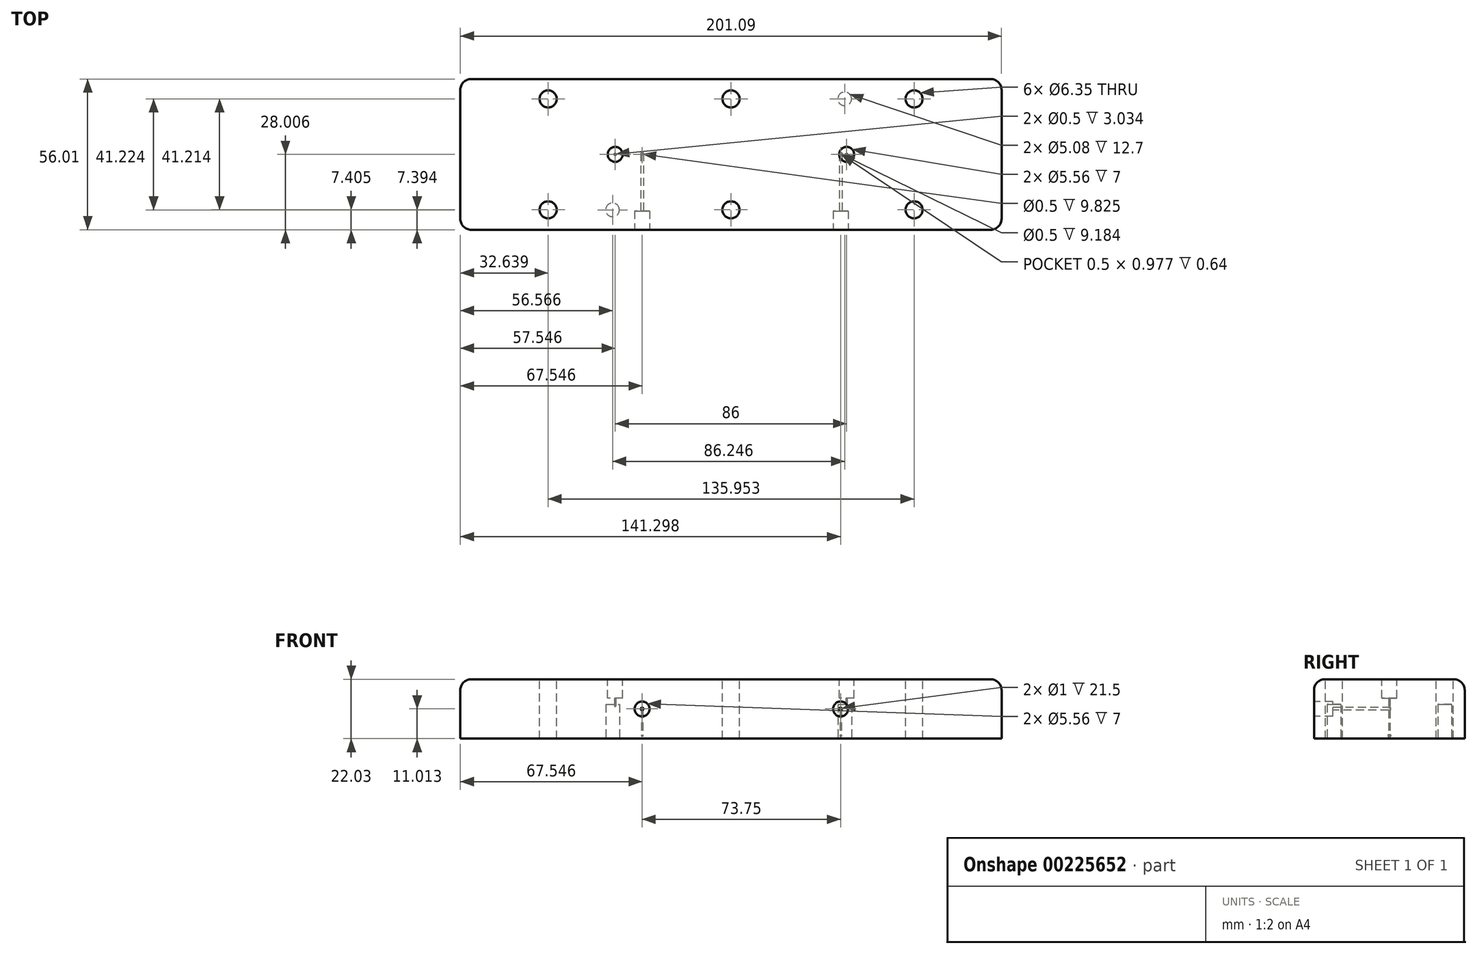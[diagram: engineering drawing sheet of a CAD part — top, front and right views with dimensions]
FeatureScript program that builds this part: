
annotation { "Feature Type Name" : "Feature", "Feature Type Description" : "" }
export const myFeature = defineFeature(function(context is Context, id is Id, definition is map)
    precondition{}
    {
        {
            var Q0;
            Q0=qCreatedBy(makeId("Top.planeOp"),FACE);
            var sketch = newSketch(context, id + "F0", { "sketchPlane" : qUnion([Q0])});
            skLineSegment(sketch, "E0.bottom", {"start": v(4.06, 0) * mm, "end": v(197.03, 0) * mm});
            skLineSegment(sketch, "E0.top", {"start": v(4.06, -56) * mm, "end": v(197.03, -56) * mm});
            skLineSegment(sketch, "E0.left", {"start": v(0, -4.06) * mm, "end": v(0, -51.94) * mm});
            skLineSegment(sketch, "E0.right", {"start": v(201.1, -4.06) * mm, "end": v(201.1, -51.94) * mm});
            skLineSegment(sketch, "E1.bottom", {"start": v(0, 0) * mm, "end": v(201.1, 0) * mm, "construction": true});
            skLineSegment(sketch, "E1.top", {"start": v(0, -7.4) * mm, "end": v(201.1, -7.4) * mm, "construction": true});
            skLineSegment(sketch, "E1.left", {"start": v(0, 0) * mm, "end": v(0, -7.4) * mm, "construction": true});
            skLineSegment(sketch, "E1.right", {"start": v(201.1, 0) * mm, "end": v(201.1, -7.4) * mm, "construction": true});
            skLineSegment(sketch, "E2.bottom", {"start": v(0, 0) * mm, "end": v(32.64, 0) * mm, "construction": true});
            skLineSegment(sketch, "E2.top", {"start": v(0, -56) * mm, "end": v(32.64, -56) * mm, "construction": true});
            skLineSegment(sketch, "E2.left", {"start": v(0, 0) * mm, "end": v(0, -56) * mm, "construction": true});
            skLineSegment(sketch, "E2.right", {"start": v(32.64, 0) * mm, "end": v(32.64, -56) * mm, "construction": true});
            skLineSegment(sketch, "E3.bottom", {"start": v(0, 0) * mm, "end": v(168.6, 0) * mm, "construction": true});
            skLineSegment(sketch, "E3.top", {"start": v(0, -56) * mm, "end": v(168.6, -56) * mm, "construction": true});
            skLineSegment(sketch, "E3.right", {"start": v(168.6, 0) * mm, "end": v(168.6, -56) * mm, "construction": true});
            skLineSegment(sketch, "E4.bottom", {"start": v(0, 0) * mm, "end": v(100.57, 0) * mm, "construction": true});
            skLineSegment(sketch, "E4.top", {"start": v(0, -56) * mm, "end": v(100.57, -56) * mm, "construction": true});
            skLineSegment(sketch, "E4.right", {"start": v(100.57, 0) * mm, "end": v(100.57, -56) * mm, "construction": true});
            skLineSegment(sketch, "E5.top", {"start": v(0, -48.6) * mm, "end": v(201.1, -48.6) * mm, "construction": true});
            skLineSegment(sketch, "E5.left", {"start": v(0, 0) * mm, "end": v(0, -48.6) * mm, "construction": true});
            skLineSegment(sketch, "E5.right", {"start": v(201.1, 0) * mm, "end": v(201.1, -48.6) * mm, "construction": true});
            skLineSegment(sketch, "E6.bottom", {"start": v(0, 0) * mm, "end": v(52.5, 0) * mm, "construction": true});
            skLineSegment(sketch, "E6.top", {"start": v(0, -56) * mm, "end": v(52.5, -56) * mm, "construction": true});
            skLineSegment(sketch, "E6.right", {"start": v(52.5, 0) * mm, "end": v(52.5, -56) * mm, "construction": true});
            skCircle(sketch, "E7", {"center": v(32.64, -7.4) * mm, "radius": 3.18 * mm});
            skCircle(sketch, "E8", {"center": v(100.57, -7.4) * mm, "radius": 3.18 * mm});
            skCircle(sketch, "E9", {"center": v(168.6, -7.4) * mm, "radius": 3.18 * mm});
            skCircle(sketch, "E10", {"center": v(168.6, -48.6) * mm, "radius": 3.18 * mm});
            skCircle(sketch, "E11", {"center": v(100.55, -48.6) * mm, "radius": 3.18 * mm});
            skCircle(sketch, "E12", {"center": v(32.64, -48.6) * mm, "radius": 3.18 * mm});
            skLineSegment(sketch, "E13.bottom", {"start": v(0, 0) * mm, "end": v(138.75, 0) * mm, "construction": true});
            skLineSegment(sketch, "E13.top", {"start": v(0, -56) * mm, "end": v(138.75, -56) * mm, "construction": true});
            skLineSegment(sketch, "E13.right", {"start": v(138.75, 0) * mm, "end": v(138.75, -56) * mm, "construction": true});
            skLineSegment(sketch, "E14.top", {"start": v(0, -56) * mm, "end": v(201.1, -56) * mm, "construction": true});
            skLineSegment(sketch, "E14.right", {"start": v(201.1, 0) * mm, "end": v(201.1, -56) * mm, "construction": true});
            skPoint(sketch, "E15.visualSharp", {"position": v(201.1, 0) * mm});
            skArc(sketch, "E15.filletArc", {"start": v(201.1, -4.06) * mm, "mid": v(199.9, -1.2) * mm, "end": v(197.03, 0) * mm});
            skPoint(sketch, "E16.visualSharp", {"position": v(0, -56) * mm});
            skArc(sketch, "E16.filletArc", {"start": v(0, -51.94) * mm, "mid": v(1.2, -54.82) * mm, "end": v(4.06, -56) * mm});
            skPoint(sketch, "E17.visualSharp", {"position": v(201.1, -56) * mm});
            skArc(sketch, "E17.filletArc", {"start": v(197.03, -56) * mm, "mid": v(199.9, -54.82) * mm, "end": v(201.1, -51.94) * mm});
            skPoint(sketch, "E18.visualSharp", {"position": v(0, 0) * mm});
            skArc(sketch, "E18.filletArc", {"start": v(4.06, 0) * mm, "mid": v(1.2, -1.2) * mm, "end": v(0, -4.06) * mm});
            skSolve(sketch);
        }
        {
            var Q0;
            Q0=qSketchRegion(id+"F0",true);
            extrude(context, id + "F1", {"entities" : qUnion([Q0]), "oppositeDirection" : true, "depth" : 22.03 * mm});
        }
        {
            var Q0;
            Q0=makeQuery(id+"F1.opExtrude","CAP_FACE",FACE,{"disambiguationData":[OSD([sQuery(id+"F0.wireOp",EDGE,"E0.bottom"),sQuery(id+"F0.wireOp",EDGE,"E0.top"),sQuery(id+"F0.wireOp",EDGE,"E0.left"),sQuery(id+"F0.wireOp",EDGE,"E0.right"),sQuery(id+"F0.wireOp",EDGE,"E7"),sQuery(id+"F0.wireOp",EDGE,"E8"),sQuery(id+"F0.wireOp",EDGE,"E9"),sQuery(id+"F0.wireOp",EDGE,"E10"),sQuery(id+"F0.wireOp",EDGE,"E11"),sQuery(id+"F0.wireOp",EDGE,"E12")])],"isStart":false});
            var sketch = newSketch(context, id + "F2", { "sketchPlane" : qUnion([Q0])});
            skLineSegment(sketch, "E19.bottom", {"start": v(4.06, 0) * mm, "end": v(201.1, 0) * mm, "construction": true});
            skLineSegment(sketch, "E19.top", {"start": v(4.06, 7.4) * mm, "end": v(201.1, 7.4) * mm, "construction": true});
            skLineSegment(sketch, "E19.left", {"start": v(4.06, 0) * mm, "end": v(4.06, 7.4) * mm, "construction": true});
            skLineSegment(sketch, "E19.right", {"start": v(201.1, 0) * mm, "end": v(201.1, 7.4) * mm, "construction": true});
            skLineSegment(sketch, "E20.top", {"start": v(4.06, 48.62) * mm, "end": v(201.1, 48.62) * mm, "construction": true});
            skLineSegment(sketch, "E20.left", {"start": v(4.06, 0) * mm, "end": v(4.06, 48.62) * mm, "construction": true});
            skLineSegment(sketch, "E20.right", {"start": v(201.1, 0) * mm, "end": v(201.1, 48.62) * mm, "construction": true});
            skLineSegment(sketch, "E21.bottom", {"start": v(4.06, 0) * mm, "end": v(56.57, 0) * mm, "construction": true});
            skLineSegment(sketch, "E21.top", {"start": v(4.06, 56) * mm, "end": v(56.57, 56) * mm, "construction": true});
            skLineSegment(sketch, "E21.left", {"start": v(4.06, 0) * mm, "end": v(4.06, 56) * mm, "construction": true});
            skLineSegment(sketch, "E21.right", {"start": v(56.57, 0) * mm, "end": v(56.57, 56) * mm, "construction": true});
            skLineSegment(sketch, "E22.bottom", {"start": v(4.06, 0) * mm, "end": v(142.81, 0) * mm, "construction": true});
            skLineSegment(sketch, "E22.top", {"start": v(4.06, 56) * mm, "end": v(142.81, 56) * mm, "construction": true});
            skLineSegment(sketch, "E22.right", {"start": v(142.81, 0) * mm, "end": v(142.81, 56) * mm, "construction": true});
            skCircle(sketch, "E23", {"center": v(56.57, 48.62) * mm, "radius": 2.54 * mm});
            skCircle(sketch, "E24", {"center": v(142.81, 7.4) * mm, "radius": 2.54 * mm});
            skSolve(sketch);
        }
        {
            var Q0;
            Q0=qSketchRegion(id+"F2",true);
            extrude(context, id + "F3", {"entities" : qUnion([Q0]), "operationType" : NewBodyOperationType.REMOVE, "oppositeDirection" : true, "depth" : 12.7 * mm});
        }
        {
            var Q0;
            Q0=makeQuery(id+"F1.opExtrude","CAP_FACE",FACE,{"disambiguationData":[OSD([sQuery(id+"F0.wireOp",EDGE,"E0.bottom"),sQuery(id+"F0.wireOp",EDGE,"E0.top"),sQuery(id+"F0.wireOp",EDGE,"E0.left"),sQuery(id+"F0.wireOp",EDGE,"E0.right"),sQuery(id+"F0.wireOp",EDGE,"E7"),sQuery(id+"F0.wireOp",EDGE,"E8"),sQuery(id+"F0.wireOp",EDGE,"E9"),sQuery(id+"F0.wireOp",EDGE,"E10"),sQuery(id+"F0.wireOp",EDGE,"E11"),sQuery(id+"F0.wireOp",EDGE,"E12"),sQuery(id+"F0.wireOp",EDGE,"E15.filletArc"),sQuery(id+"F0.wireOp",EDGE,"E16.filletArc"),sQuery(id+"F0.wireOp",EDGE,"E17.filletArc"),sQuery(id+"F0.wireOp",EDGE,"E18.filletArc")])],"isStart":false});
            var sketch = newSketch(context, id + "F4", { "sketchPlane" : qUnion([Q0])});
            skLineSegment(sketch, "E25.bottom", {"start": v(143.55, 35.5) * mm, "end": v(57.55, 35.5) * mm, "construction": true});
            skLineSegment(sketch, "E25.top", {"start": v(143.55, 20.5) * mm, "end": v(57.55, 20.5) * mm, "construction": true});
            skLineSegment(sketch, "E25.left", {"start": v(143.55, 35.5) * mm, "end": v(143.55, 20.5) * mm, "construction": true});
            skLineSegment(sketch, "E25.right", {"start": v(57.55, 35.5) * mm, "end": v(57.55, 20.5) * mm, "construction": true});
            skPoint(sketch, "E25.middle", {"position": v(100.55, 28) * mm});
            skPoint(sketch, "E25.middle.positionSnap0", {"position": v(100.55, 56) * mm});
            skPoint(sketch, "E25.middle.positionSnap1", {"position": v(0, 28) * mm});
            skPoint(sketch, "E25.centerSnap0", {"position": v(100.55, 56) * mm});
            skPoint(sketch, "E25.centerSnap1", {"position": v(0, 28) * mm});
            skCircle(sketch, "E26", {"center": v(143.55, 28) * mm, "radius": 0.25 * mm, "construction": true});
            skCircle(sketch, "E27", {"center": v(57.55, 28) * mm, "radius": 0.25 * mm, "construction": true});
            skLineSegment(sketch, "E28.bottom", {"start": v(57.55, 35.5) * mm, "end": v(67.55, 35.5) * mm, "construction": true});
            skLineSegment(sketch, "E28.top", {"start": v(57.55, 20.5) * mm, "end": v(67.55, 20.5) * mm, "construction": true});
            skLineSegment(sketch, "E28.right", {"start": v(67.55, 35.5) * mm, "end": v(67.55, 20.5) * mm, "construction": true});
            skLineSegment(sketch, "E29", {"start": v(67.55, 35.5) * mm, "end": v(143.55, 28.25) * mm, "construction": true});
            skLineSegment(sketch, "E30", {"start": v(67.55, 20.5) * mm, "end": v(143.55, 27.75) * mm, "construction": true});
            skLineSegment(sketch, "E31.bottom", {"start": v(143.55, 35.5) * mm, "end": v(141.55, 35.5) * mm, "construction": true});
            skLineSegment(sketch, "E31.top", {"start": v(143.55, 20.5) * mm, "end": v(141.55, 20.5) * mm, "construction": true});
            skLineSegment(sketch, "E31.right", {"start": v(141.55, 35.5) * mm, "end": v(141.55, 20.5) * mm, "construction": true});
            skLineSegment(sketch, "E32.bottom", {"start": v(141.55, 35.5) * mm, "end": v(141.05, 35.5) * mm, "construction": true});
            skLineSegment(sketch, "E32.top", {"start": v(141.55, 20.5) * mm, "end": v(141.05, 20.5) * mm, "construction": true});
            skLineSegment(sketch, "E32.right", {"start": v(141.05, 35.5) * mm, "end": v(141.05, 20.5) * mm, "construction": true});
            skLineSegment(sketch, "E33", {"start": v(141.05, 28.5) * mm, "end": v(141.55, 28.44) * mm});
            skLineSegment(sketch, "E34", {"start": v(141.55, 28.44) * mm, "end": v(141.55, 27.56) * mm});
            skLineSegment(sketch, "E35", {"start": v(141.55, 27.56) * mm, "end": v(141.05, 27.52) * mm});
            skLineSegment(sketch, "E36", {"start": v(141.05, 27.52) * mm, "end": v(141.05, 28.5) * mm});
            skSolve(sketch);
        }
        {
            var Q0;
            Q0 = qSketchRegion(id + "F4", true);
            extrude(context, id + "F5", {"entities" : qUnion([Q0]), "operationType" : NewBodyOperationType.REMOVE, "oppositeDirection" : true, "depth" : 1.4 * mm});
        }
        {
            var Q0;
            Q0=makeQuery(id+"F1.opExtrude","CAP_FACE",FACE,{"disambiguationData":[OSD([sQuery(id+"F0.wireOp",EDGE,"E0.bottom"),sQuery(id+"F0.wireOp",EDGE,"E0.top"),sQuery(id+"F0.wireOp",EDGE,"E0.left"),sQuery(id+"F0.wireOp",EDGE,"E0.right"),sQuery(id+"F0.wireOp",EDGE,"E7"),sQuery(id+"F0.wireOp",EDGE,"E8"),sQuery(id+"F0.wireOp",EDGE,"E9"),sQuery(id+"F0.wireOp",EDGE,"E10"),sQuery(id+"F0.wireOp",EDGE,"E11"),sQuery(id+"F0.wireOp",EDGE,"E12"),sQuery(id+"F0.wireOp",EDGE,"E15.filletArc"),sQuery(id+"F0.wireOp",EDGE,"E16.filletArc"),sQuery(id+"F0.wireOp",EDGE,"E17.filletArc"),sQuery(id+"F0.wireOp",EDGE,"E18.filletArc")])],"isStart":false});
            var sketch = newSketch(context, id + "F6", { "sketchPlane" : qUnion([Q0])});
            skLineSegment(sketch, "E37.bottom", {"start": v(143.55, 35.5) * mm, "end": v(57.55, 35.5) * mm, "construction": true});
            skLineSegment(sketch, "E37.top", {"start": v(143.55, 20.5) * mm, "end": v(57.55, 20.5) * mm, "construction": true});
            skLineSegment(sketch, "E37.left", {"start": v(143.55, 35.5) * mm, "end": v(143.55, 20.5) * mm, "construction": true});
            skLineSegment(sketch, "E37.right", {"start": v(57.55, 35.5) * mm, "end": v(57.55, 20.5) * mm, "construction": true});
            skPoint(sketch, "E37.middle", {"position": v(100.55, 28) * mm});
            skPoint(sketch, "E37.middle.positionSnap0", {"position": v(100.55, 56) * mm});
            skPoint(sketch, "E37.middle.positionSnap1", {"position": v(0, 28) * mm});
            skPoint(sketch, "E37.centerSnap0", {"position": v(100.55, 56) * mm});
            skPoint(sketch, "E37.centerSnap1", {"position": v(0, 28) * mm});
            skLineSegment(sketch, "E38.bottom", {"start": v(57.55, 35.5) * mm, "end": v(67.55, 35.5) * mm, "construction": true});
            skLineSegment(sketch, "E38.top", {"start": v(57.55, 20.5) * mm, "end": v(67.55, 20.5) * mm, "construction": true});
            skLineSegment(sketch, "E38.right", {"start": v(67.55, 35.5) * mm, "end": v(67.55, 20.5) * mm, "construction": true});
            skArc(sketch, "E39", {"start": v(57.4, 28.2) * mm, "mid": v(57.3, 28) * mm, "end": v(57.4, 27.8) * mm});
            skArc(sketch, "E40", {"start": v(143.55, 27.75) * mm, "mid": v(143.8, 28) * mm, "end": v(143.55, 28.25) * mm});
            skLineSegment(sketch, "E41", {"start": v(67.55, 35.5) * mm, "end": v(57.4, 28.2) * mm});
            skLineSegment(sketch, "E42", {"start": v(67.55, 20.5) * mm, "end": v(57.4, 27.8) * mm});
            skLineSegment(sketch, "E43", {"start": v(67.55, 35.5) * mm, "end": v(143.55, 28.25) * mm});
            skLineSegment(sketch, "E44", {"start": v(67.55, 20.5) * mm, "end": v(143.55, 27.75) * mm});
            skSolve(sketch);
        }
        {
            var Q0;
            Q0 = qSketchRegion(id + "F6", true);
            extrude(context, id + "F7", {"entities" : qUnion([Q0]), "operationType" : NewBodyOperationType.REMOVE, "oppositeDirection" : true, "depth" : .4 * mm});
        }
        {
            var Q0;
            Q0=makeQuery(id+"F1.opExtrude","CAP_FACE",FACE,{"disambiguationData":[OSD([sQuery(id+"F0.wireOp",EDGE,"E0.bottom"),sQuery(id+"F0.wireOp",EDGE,"E0.top"),sQuery(id+"F0.wireOp",EDGE,"E0.left"),sQuery(id+"F0.wireOp",EDGE,"E0.right"),sQuery(id+"F0.wireOp",EDGE,"E7"),sQuery(id+"F0.wireOp",EDGE,"E8"),sQuery(id+"F0.wireOp",EDGE,"E9"),sQuery(id+"F0.wireOp",EDGE,"E10"),sQuery(id+"F0.wireOp",EDGE,"E11"),sQuery(id+"F0.wireOp",EDGE,"E12"),sQuery(id+"F0.wireOp",EDGE,"E15.filletArc"),sQuery(id+"F0.wireOp",EDGE,"E16.filletArc"),sQuery(id+"F0.wireOp",EDGE,"E17.filletArc"),sQuery(id+"F0.wireOp",EDGE,"E18.filletArc")])],"isStart":false});
            var sketch = newSketch(context, id + "F8", { "sketchPlane" : qUnion([Q0])});
            skLineSegment(sketch, "E45.bottom", {"start": v(143.55, 20.5) * mm, "end": v(57.55, 20.5) * mm, "construction": true});
            skLineSegment(sketch, "E45.top", {"start": v(143.55, 35.5) * mm, "end": v(57.55, 35.5) * mm, "construction": true});
            skLineSegment(sketch, "E45.left", {"start": v(143.55, 20.5) * mm, "end": v(143.55, 27.75) * mm, "construction": true});
            skLineSegment(sketch, "E45.right", {"start": v(57.55, 20.5) * mm, "end": v(57.55, 35.5) * mm, "construction": true});
            skPoint(sketch, "E45.middle", {"position": v(100.55, 28) * mm});
            skPoint(sketch, "E45.middle.positionSnap0", {"position": v(100.55, 56) * mm});
            skPoint(sketch, "E45.middle.positionSnap1", {"position": v(0, 28) * mm});
            skPoint(sketch, "E45.centerSnap0", {"position": v(100.55, 56) * mm});
            skPoint(sketch, "E45.centerSnap1", {"position": v(0, 28) * mm});
            skLineSegment(sketch, "E46.bottom", {"start": v(57.55, 35.5) * mm, "end": v(67.55, 35.5) * mm, "construction": true});
            skLineSegment(sketch, "E46.top", {"start": v(57.55, 20.5) * mm, "end": v(67.55, 20.5) * mm, "construction": true});
            skLineSegment(sketch, "E46.left", {"start": v(57.55, 35.5) * mm, "end": v(57.55, 20.5) * mm, "construction": true});
            skArc(sketch, "E47", {"start": v(57.4, 28.2) * mm, "mid": v(57.3, 28) * mm, "end": v(57.4, 27.8) * mm});
            skLineSegment(sketch, "E48", {"start": v(67.55, 35.5) * mm, "end": v(57.4, 28.2) * mm});
            skLineSegment(sketch, "E49", {"start": v(67.55, 20.5) * mm, "end": v(57.4, 27.8) * mm});
            skLineSegment(sketch, "E50", {"start": v(67.55, 35.5) * mm, "end": v(141.55, 28.45) * mm});
            skLineSegment(sketch, "E51", {"start": v(67.55, 20.5) * mm, "end": v(141.55, 27.56) * mm});
            skLineSegment(sketch, "E52", {"start": v(143.55, 27.75) * mm, "end": v(143.55, 27.75) * mm});
            skLineSegment(sketch, "E53.trimOffspring", {"start": v(143.55, 28.25) * mm, "end": v(143.55, 35.5) * mm, "construction": true});
            skLineSegment(sketch, "E54.trimOffspring", {"start": v(143.55, 28.25) * mm, "end": v(143.55, 28.25) * mm});
            skLineSegment(sketch, "E55.bottom", {"start": v(143.55, 35.5) * mm, "end": v(141.55, 35.5) * mm, "construction": true});
            skLineSegment(sketch, "E55.top", {"start": v(143.55, 20.5) * mm, "end": v(141.55, 20.5) * mm, "construction": true});
            skLineSegment(sketch, "E55.left", {"start": v(143.55, 35.5) * mm, "end": v(143.55, 20.5) * mm, "construction": true});
            skLineSegment(sketch, "E55.right", {"start": v(141.55, 35.5) * mm, "end": v(141.55, 20.5) * mm, "construction": true});
            skLineSegment(sketch, "E56", {"start": v(141.55, 28.45) * mm, "end": v(141.55, 27.56) * mm});
            skPoint(sketch, "E57.center.orphan", {"position": v(143.55, 28) * mm});
            skSolve(sketch);
        }
        {
            var Q0;
            Q0=qSketchRegion(id+"F8",true);
            extrude(context, id + "F9", {"entities" : qUnion([Q0]), "operationType" : NewBodyOperationType.REMOVE, "oppositeDirection" : true, "depth" : .4 * mm});
        }
        {
            var Q0;
            Q0=makeQuery(id+"F1.opExtrude","CAP_FACE",FACE,{"disambiguationData":[OSD([sQuery(id+"F0.wireOp",EDGE,"E0.bottom"),sQuery(id+"F0.wireOp",EDGE,"E0.top"),sQuery(id+"F0.wireOp",EDGE,"E0.left"),sQuery(id+"F0.wireOp",EDGE,"E0.right"),sQuery(id+"F0.wireOp",EDGE,"E7"),sQuery(id+"F0.wireOp",EDGE,"E8"),sQuery(id+"F0.wireOp",EDGE,"E9"),sQuery(id+"F0.wireOp",EDGE,"E10"),sQuery(id+"F0.wireOp",EDGE,"E11"),sQuery(id+"F0.wireOp",EDGE,"E12"),sQuery(id+"F0.wireOp",EDGE,"E15.filletArc"),sQuery(id+"F0.wireOp",EDGE,"E16.filletArc"),sQuery(id+"F0.wireOp",EDGE,"E17.filletArc"),sQuery(id+"F0.wireOp",EDGE,"E18.filletArc")])],"isStart":false});
            var sketch = newSketch(context, id + "F10", { "sketchPlane" : qUnion([Q0])});
            skCircle(sketch, "E58", {"center": v(57.55, 28) * mm, "radius": 0.25 * mm});
            skCircle(sketch, "E59", {"center": v(143.55, 28) * mm, "radius": 0.25 * mm});
            skSolve(sketch);
        }
        {
            var Q0;
            Q0 = qSketchRegion(id + "F10", true);
            extrude(context, id + "F11", {"entities" : qUnion([Q0]), "operationType" : NewBodyOperationType.REMOVE, "endBound" : BoundingType.THROUGH_ALL, "oppositeDirection" : true, "depth" : 25 * mm});
        }
        {
            var Q0;
            Q0=makeQuery(id+"F1.opExtrude","CAP_FACE",FACE,{"disambiguationData":[OSD([sQuery(id+"F0.wireOp",EDGE,"E0.bottom"),sQuery(id+"F0.wireOp",EDGE,"E0.top"),sQuery(id+"F0.wireOp",EDGE,"E0.left"),sQuery(id+"F0.wireOp",EDGE,"E0.right"),sQuery(id+"F0.wireOp",EDGE,"E7"),sQuery(id+"F0.wireOp",EDGE,"E8"),sQuery(id+"F0.wireOp",EDGE,"E9"),sQuery(id+"F0.wireOp",EDGE,"E10"),sQuery(id+"F0.wireOp",EDGE,"E11"),sQuery(id+"F0.wireOp",EDGE,"E12"),sQuery(id+"F0.wireOp",EDGE,"E15.filletArc"),sQuery(id+"F0.wireOp",EDGE,"E16.filletArc"),sQuery(id+"F0.wireOp",EDGE,"E17.filletArc"),sQuery(id+"F0.wireOp",EDGE,"E18.filletArc")])],"isStart":false});
            var sketch = newSketch(context, id + "F12", { "sketchPlane" : qUnion([Q0])});
            skLineSegment(sketch, "E60", {"start": v(67.55, 35.5) * mm, "end": v(67.55, 20.5) * mm, "construction": true});
            skCircle(sketch, "E61", {"center": v(67.55, 28) * mm, "radius": 0.25 * mm});
            skLineSegment(sketch, "E62", {"start": v(141.55, 27.56) * mm, "end": v(141.55, 28.44) * mm, "construction": true});
            skLineSegment(sketch, "E63", {"start": v(141.05, 27.52) * mm, "end": v(141.05, 28.5) * mm, "construction": true});
            skLineSegment(sketch, "E64", {"start": v(141.05, 28) * mm, "end": v(141.55, 28) * mm, "construction": true});
            skCircle(sketch, "E65", {"center": v(141.3, 28) * mm, "radius": 0.25 * mm});
            skSolve(sketch);
        }
        {
            var Q0;
            Q0 = qSketchRegion(id + "F12", true);
            extrude(context, id + "F13", {"entities" : qUnion([Q0]), "operationType" : NewBodyOperationType.REMOVE, "oppositeDirection" : true, "depth" : 11.5 * mm});
        }
        {
            var Q0;
            Q0=makeQuery(id+"F1.opExtrude","SWEPT_FACE",FACE,{"disambiguationData":[OSD([sQuery(id+"F0.wireOp",EDGE,"E0.top")])]});
            var sketch = newSketch(context, id + "F14", { "sketchPlane" : qUnion([Q0])});
            skLineSegment(sketch, "E66.bottom", {"start": v(143.55, -16.02) * mm, "end": v(57.55, -16.02) * mm, "construction": true});
            skLineSegment(sketch, "E66.top", {"start": v(143.55, -6.02) * mm, "end": v(57.55, -6.02) * mm, "construction": true});
            skLineSegment(sketch, "E66.left", {"start": v(143.55, -16.02) * mm, "end": v(143.55, -6.02) * mm, "construction": true});
            skLineSegment(sketch, "E66.right", {"start": v(57.55, -16.02) * mm, "end": v(57.55, -6.02) * mm, "construction": true});
            skPoint(sketch, "E66.middle", {"position": v(100.55, -11.02) * mm});
            skPoint(sketch, "E66.middle.positionSnap0", {"position": v(100.55, 0) * mm});
            skPoint(sketch, "E66.middle.positionSnap1", {"position": v(4.06, -11.02) * mm});
            skPoint(sketch, "E66.centerSnap0", {"position": v(100.55, 0) * mm});
            skPoint(sketch, "E66.centerSnap1", {"position": v(4.06, -11.02) * mm});
            skLineSegment(sketch, "E67.bottom", {"start": v(57.55, -6.02) * mm, "end": v(67.55, -6.02) * mm, "construction": true});
            skLineSegment(sketch, "E67.top", {"start": v(57.55, -16.02) * mm, "end": v(67.55, -16.02) * mm, "construction": true});
            skLineSegment(sketch, "E67.left", {"start": v(57.55, -6.02) * mm, "end": v(57.55, -16.02) * mm, "construction": true});
            skLineSegment(sketch, "E67.right", {"start": v(67.55, -6.02) * mm, "end": v(67.55, -16.02) * mm, "construction": true});
            skLineSegment(sketch, "E68.bottom", {"start": v(143.55, -6.02) * mm, "end": v(141.3, -6.02) * mm, "construction": true});
            skLineSegment(sketch, "E68.top", {"start": v(143.55, -16.02) * mm, "end": v(141.3, -16.02) * mm, "construction": true});
            skLineSegment(sketch, "E68.left", {"start": v(143.55, -6.02) * mm, "end": v(143.55, -16.02) * mm, "construction": true});
            skLineSegment(sketch, "E68.right", {"start": v(141.3, -6.02) * mm, "end": v(141.3, -16.02) * mm, "construction": true});
            skCircle(sketch, "E69", {"center": v(141.3, -11.02) * mm, "radius": 0.5 * mm});
            skCircle(sketch, "E70", {"center": v(67.55, -11.02) * mm, "radius": 0.5 * mm});
            skSolve(sketch);
        }
        {
            var Q0;
            Q0 = qSketchRegion(id + "F14", true);
            extrude(context, id + "F15", {"entities" : qUnion([Q0]), "operationType" : NewBodyOperationType.REMOVE, "oppositeDirection" : true, "depth" : 28.5 * mm});
        }
        {
            var Q0;
            Q0=makeQuery(id+"F1.opExtrude","SWEPT_FACE",FACE,{"disambiguationData":[OSD([sQuery(id+"F0.wireOp",EDGE,"E0.top")])]});
            var sketch = newSketch(context, id + "F16", { "sketchPlane" : qUnion([Q0])});
            skCircle(sketch, "E71", {"center": v(67.55, -11.02) * mm, "radius": 2.78 * mm});
            skCircle(sketch, "E72", {"center": v(141.3, -11.02) * mm, "radius": 2.78 * mm});
            skSolve(sketch);
        }
        {
            var Q0;
            Q0 = qSketchRegion(id + "F16", true);
            extrude(context, id + "F17", {"entities" : qUnion([Q0]), "operationType" : NewBodyOperationType.REMOVE, "oppositeDirection" : true, "depth" : 7 * mm});
        }
        {
            var Q0;
            Q0=makeQuery(id+"F1.opExtrude","CAP_EDGE",EDGE,{"disambiguationData":[OSD([sQuery(id+"F0.wireOp",EDGE,"E0.top")])],"isStart":true});
            var Q1;
            Q1=makeQuery(id+"F1.opExtrude","CAP_EDGE",EDGE,{"disambiguationData":[OSD([sQuery(id+"F0.wireOp",EDGE,"E17.filletArc")])],"isStart":true});
            var Q2;
            Q2=makeQuery(id+"F1.opExtrude","CAP_EDGE",EDGE,{"disambiguationData":[OSD([sQuery(id+"F0.wireOp",EDGE,"E0.right")])],"isStart":true});
            var Q3;
            Q3=makeQuery(id+"F1.opExtrude","CAP_EDGE",EDGE,{"disambiguationData":[OSD([sQuery(id+"F0.wireOp",EDGE,"E15.filletArc")])],"isStart":true});
            var Q4;
            Q4=makeQuery(id+"F1.opExtrude","CAP_EDGE",EDGE,{"disambiguationData":[OSD([sQuery(id+"F0.wireOp",EDGE,"E0.bottom")])],"isStart":true});
            var Q5;
            Q5=makeQuery(id+"F1.opExtrude","CAP_EDGE",EDGE,{"disambiguationData":[OSD([sQuery(id+"F0.wireOp",EDGE,"E18.filletArc")])],"isStart":true});
            var Q6;
            Q6=makeQuery(id+"F1.opExtrude","CAP_EDGE",EDGE,{"disambiguationData":[OSD([sQuery(id+"F0.wireOp",EDGE,"E0.left")])],"isStart":true});
            var Q7;
            Q7=makeQuery(id+"F1.opExtrude","CAP_EDGE",EDGE,{"disambiguationData":[OSD([sQuery(id+"F0.wireOp",EDGE,"E16.filletArc")])],"isStart":true});
            fillet(context, id + "F18", {"entities" : qUnion([Q0, Q1, Q2, Q3, Q4, Q5, Q6, Q7]), "radius" : 4.06 * mm, "tangentPropagation" : true, "allowEdgeOverflow" : false});
        }
        {
            var Q0;
            Q0=makeQuery(id+"F1.opExtrude","CAP_FACE",FACE,{"disambiguationData":[OSD([sQuery(id+"F0.wireOp",EDGE,"E0.bottom"),sQuery(id+"F0.wireOp",EDGE,"E0.top"),sQuery(id+"F0.wireOp",EDGE,"E0.left"),sQuery(id+"F0.wireOp",EDGE,"E0.right"),sQuery(id+"F0.wireOp",EDGE,"E7"),sQuery(id+"F0.wireOp",EDGE,"E8"),sQuery(id+"F0.wireOp",EDGE,"E9"),sQuery(id+"F0.wireOp",EDGE,"E10"),sQuery(id+"F0.wireOp",EDGE,"E11"),sQuery(id+"F0.wireOp",EDGE,"E12"),sQuery(id+"F0.wireOp",EDGE,"E15.filletArc"),sQuery(id+"F0.wireOp",EDGE,"E16.filletArc"),sQuery(id+"F0.wireOp",EDGE,"E17.filletArc"),sQuery(id+"F0.wireOp",EDGE,"E18.filletArc")])],"isStart":true});
            var sketch = newSketch(context, id + "F19", { "sketchPlane" : qUnion([Q0])});
            skCircle(sketch, "E73", {"center": v(57.55, -28) * mm, "radius": 2.78 * mm});
            skCircle(sketch, "E74", {"center": v(143.55, -28) * mm, "radius": 2.78 * mm});
            skSolve(sketch);
        }
        {
            var Q0;
            Q0 = qSketchRegion(id + "F19", true);
            extrude(context, id + "F20", {"entities" : qUnion([Q0]), "operationType" : NewBodyOperationType.REMOVE, "oppositeDirection" : true, "depth" : 7 * mm});
        }
        {
            var Q0;
            Q0=makeQuery(id+"F1.opExtrude","CAP_FACE",FACE,{"disambiguationData":[OSD([sQuery(id+"F0.wireOp",EDGE,"E0.bottom"),sQuery(id+"F0.wireOp",EDGE,"E0.top"),sQuery(id+"F0.wireOp",EDGE,"E0.left"),sQuery(id+"F0.wireOp",EDGE,"E0.right"),sQuery(id+"F0.wireOp",EDGE,"E7"),sQuery(id+"F0.wireOp",EDGE,"E8"),sQuery(id+"F0.wireOp",EDGE,"E9"),sQuery(id+"F0.wireOp",EDGE,"E10"),sQuery(id+"F0.wireOp",EDGE,"E11"),sQuery(id+"F0.wireOp",EDGE,"E12"),sQuery(id+"F0.wireOp",EDGE,"E15.filletArc"),sQuery(id+"F0.wireOp",EDGE,"E16.filletArc"),sQuery(id+"F0.wireOp",EDGE,"E17.filletArc"),sQuery(id+"F0.wireOp",EDGE,"E18.filletArc")])],"isStart":false});
            var sketch = newSketch(context, id + "F21", { "sketchPlane" : qUnion([Q0])});
            skLineSegment(sketch, "E75", {"start": v(67.55, 35.5) * mm, "end": v(57.4, 28.2) * mm});
            skPoint(sketch, "E76.center.orphan", {"position": v(57.55, 28) * mm});
            skArc(sketch, "E77", {"start": v(57.4, 28.2) * mm, "mid": v(57.3, 28) * mm, "end": v(57.4, 27.8) * mm});
            skLineSegment(sketch, "E78", {"start": v(67.55, 20.5) * mm, "end": v(57.4, 27.8) * mm});
            skArc(sketch, "E79", {"start": v(143.55, 27.75) * mm, "mid": v(143.8, 28) * mm, "end": v(143.55, 28.25) * mm});
            skLineSegment(sketch, "E80", {"start": v(67.55, 35.5) * mm, "end": v(143.55, 28.25) * mm});
            skLineSegment(sketch, "E81", {"start": v(67.55, 20.5) * mm, "end": v(143.55, 27.75) * mm});
            skSolve(sketch);
        }
        {
            var Q0;
            Q0 = qSketchRegion(id + "F21", true);
            extrude(context, id + "F22", {"entities" : qUnion([Q0]), "oppositeDirection" : true, "depth" : .4 * mm});
        }
        {
            var Q0;
            Q0=makeQuery(id+"F22.opExtrude","CAP_FACE",FACE,{"disambiguationData":[OSD([sQuery(id+"F21.wireOp",EDGE,"E75"),sQuery(id+"F21.wireOp",EDGE,"E77"),sQuery(id+"F21.wireOp",EDGE,"E78"),sQuery(id+"F21.wireOp",EDGE,"E79"),sQuery(id+"F21.wireOp",EDGE,"E80"),sQuery(id+"F21.wireOp",EDGE,"E81")])],"isStart":false});
            var sketch = newSketch(context, id + "F23", { "sketchPlane" : qUnion([Q0])});
            skArc(sketch, "E82", {"start": v(57.4, -27.8) * mm, "mid": v(57.3, -28) * mm, "end": v(57.4, -28.2) * mm});
            skArc(sketch, "E83", {"start": v(143.55, -28.25) * mm, "mid": v(143.8, -28) * mm, "end": v(143.55, -27.75) * mm});
            skLineSegment(sketch, "E84", {"start": v(67.55, -20.5) * mm, "end": v(57.4, -27.8) * mm});
            skLineSegment(sketch, "E85", {"start": v(67.55, -35.5) * mm, "end": v(57.4, -28.2) * mm});
            skLineSegment(sketch, "E86", {"start": v(67.55, -20.5) * mm, "end": v(143.55, -27.75) * mm});
            skLineSegment(sketch, "E87", {"start": v(67.55, -35.5) * mm, "end": v(143.55, -28.25) * mm});
            skSolve(sketch);
        }
        {
            var Q0;
            Q0 = qSketchRegion(id + "F23", true);
            extrude(context, id + "F24", {"entities" : qUnion([Q0]), "operationType" : NewBodyOperationType.ADD, "depth" : .36 * mm});
        }
        {
            var Q0;
            Q0=makeQuery(id+"F22.opExtrude","CAP_FACE",FACE,{"disambiguationData":[OSD([sQuery(id+"F21.wireOp",EDGE,"E75"),sQuery(id+"F21.wireOp",EDGE,"E77"),sQuery(id+"F21.wireOp",EDGE,"E78"),sQuery(id+"F21.wireOp",EDGE,"E79"),sQuery(id+"F21.wireOp",EDGE,"E80"),sQuery(id+"F21.wireOp",EDGE,"E81")])],"isStart":true});
            var sketch = newSketch(context, id + "F25", { "sketchPlane" : qUnion([Q0])});
            skCircle(sketch, "E88", {"center": v(57.55, 28) * mm, "radius": 0.25 * mm});
            skCircle(sketch, "E89", {"center": v(143.55, 28) * mm, "radius": 0.25 * mm});
            skSolve(sketch);
        }
        {
            var Q0;
            Q0 = qSketchRegion(id + "F25", true);
            extrude(context, id + "F26", {"entities" : qUnion([Q0]), "operationType" : NewBodyOperationType.ADD, "oppositeDirection" : true, "depth" : 12 * mm});
        }
    });
